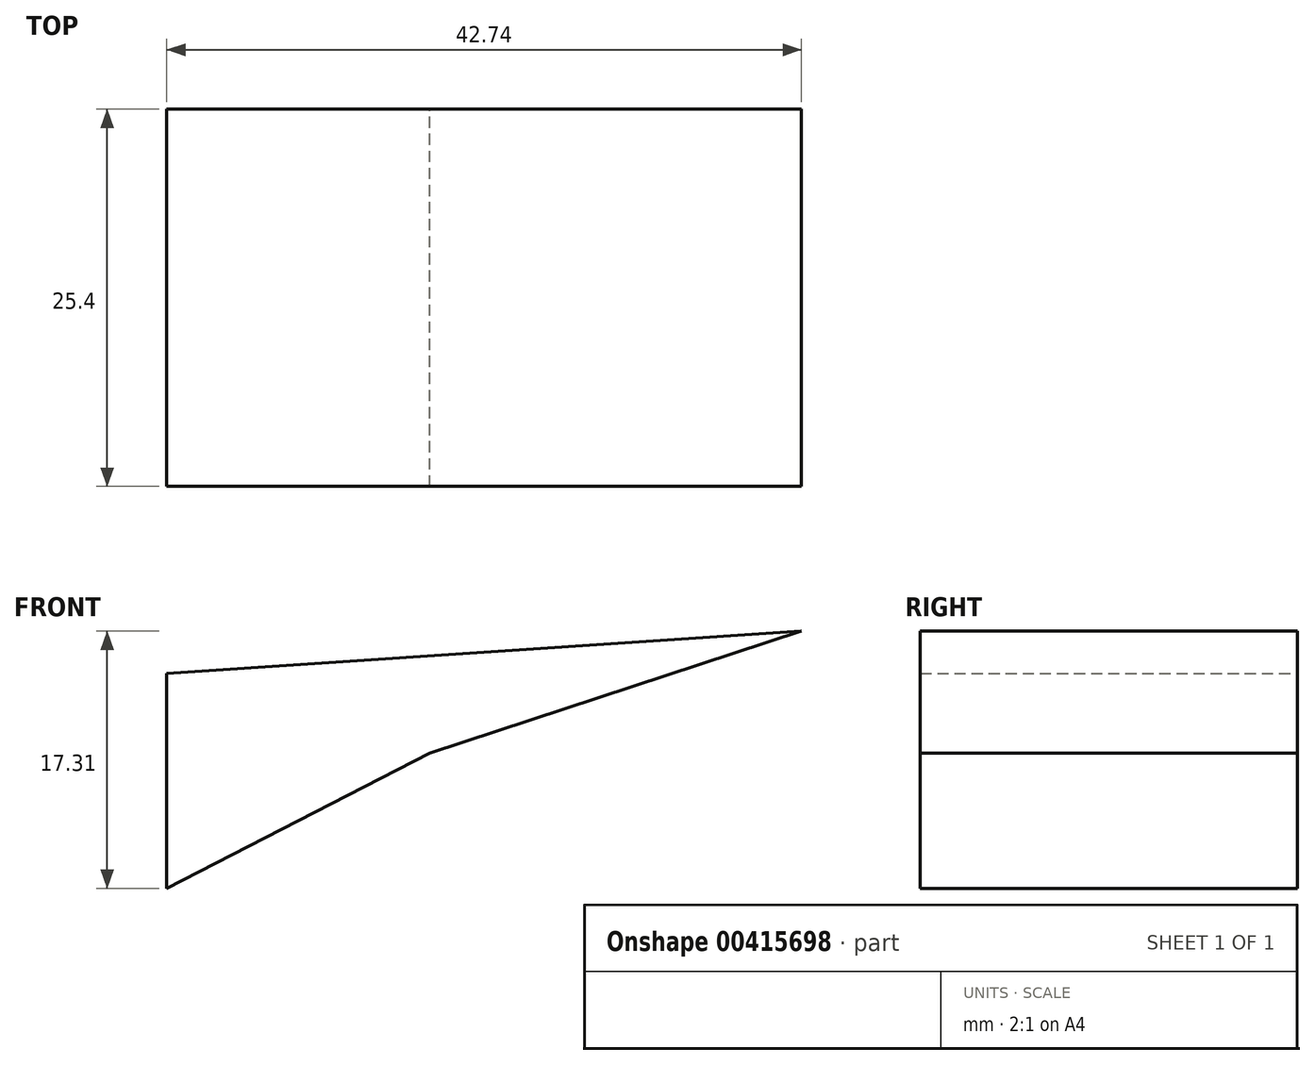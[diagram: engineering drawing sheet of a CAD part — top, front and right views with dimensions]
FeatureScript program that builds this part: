
annotation { "Feature Type Name" : "Feature", "Feature Type Description" : "" }
export const myFeature = defineFeature(function(context is Context, id is Id, definition is map)
    precondition{}
    {
        {
            var Q0;
            Q0=qCreatedBy(makeId("Front.planeOp"),FACE);
            var sketch = newSketch(context, id + "F0", { "sketchPlane" : qUnion([Q0])});
            skLineSegment(sketch, "E0", {"start": v(-67.1, 18.76) * mm, "end": v(-67.1, 4.3) * mm});
            skLineSegment(sketch, "E1", {"start": v(-67.1, 4.3) * mm, "end": v(-49.39, 13.4) * mm});
            skLineSegment(sketch, "E2", {"start": v(-49.39, 13.4) * mm, "end": v(-67.1, 18.76) * mm});
            skLineSegment(sketch, "E3", {"start": v(-49.39, 13.4) * mm, "end": v(-24.35, 21.62) * mm});
            skLineSegment(sketch, "E4", {"start": v(-24.35, 21.62) * mm, "end": v(-67.1, 18.76) * mm});
            skLineSegment(sketch, "E5", {"start": v(0, 0) * mm, "end": v(-67.1, 4.3) * mm});
            skLineSegment(sketch, "E6", {"start": v(23.4, 21.62) * mm, "end": v(-49.39, 13.4) * mm});
            skSolve(sketch);
        }
        {
            var Q0;
            Q0=makeQuery(id+"F0.imprint","IMPRINT",FACE,{"disambiguationData":[TD([[makeQuery(id+"F0.imprint","IMPRINT",EDGE,{"derivedFrom":sQuery(id+"F0.wireOp",EDGE,"E0")}),1.0]])]});
            var Q1;
            Q1=makeQuery(id+"F0.imprint","IMPRINT",FACE,{"disambiguationData":[TD([[makeQuery(id+"F0.imprint","IMPRINT",EDGE,{"derivedFrom":sQuery(id+"F0.wireOp",EDGE,"E2")}),-1.0]])]});
            extrude(context, id + "F1", {"entities" : qUnion([Q0, Q1]), "depth" : 25.4 * mm});
        }
    });
